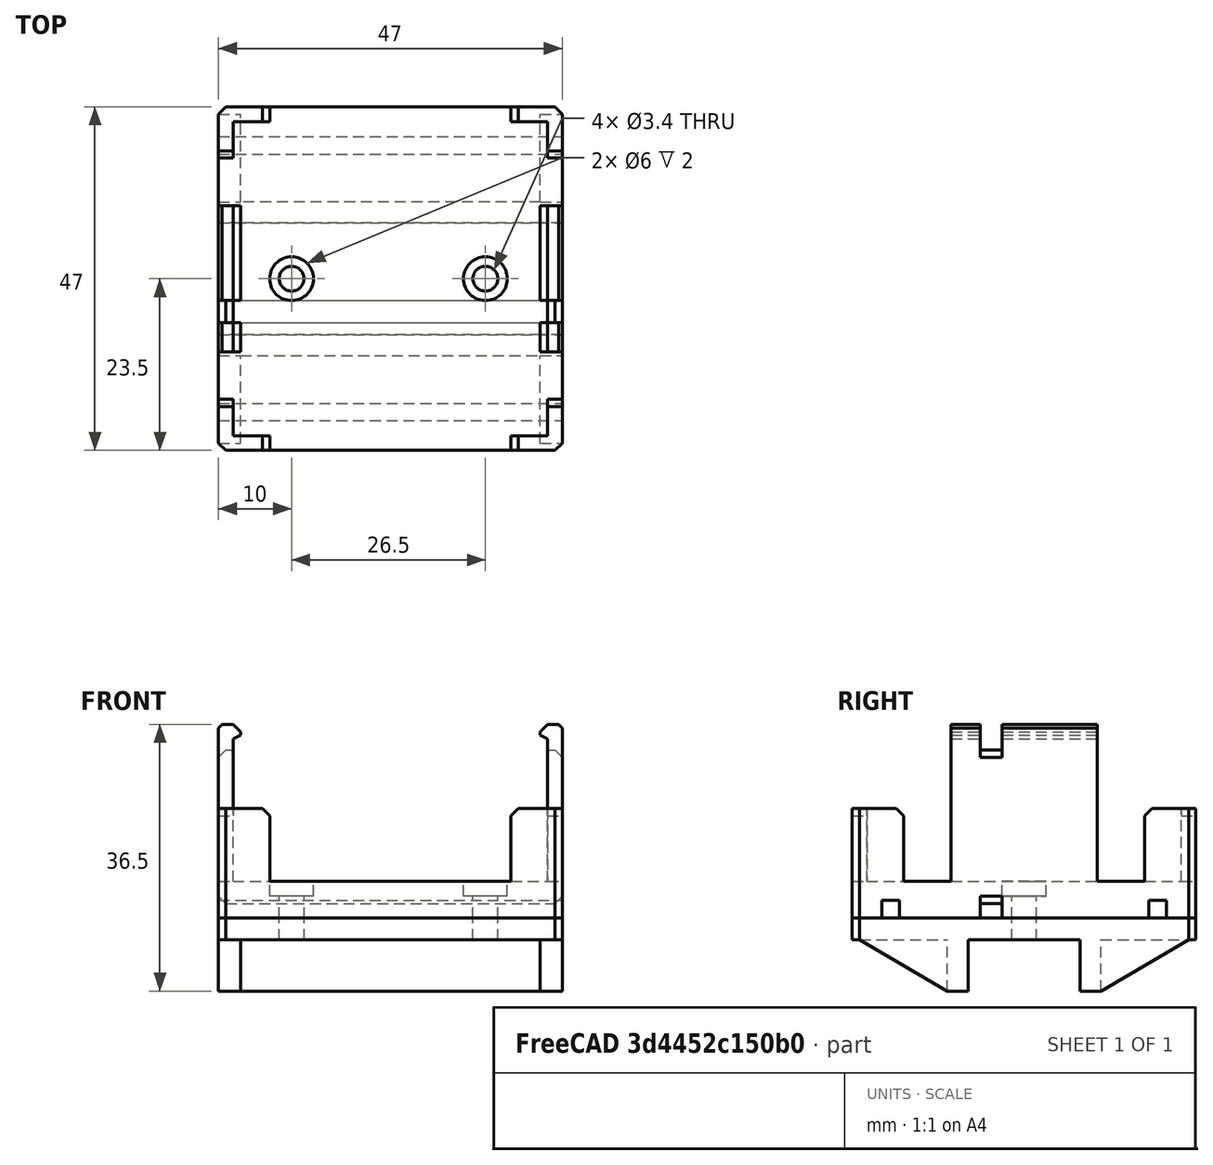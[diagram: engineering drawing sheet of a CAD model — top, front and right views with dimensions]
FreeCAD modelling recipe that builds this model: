
FCSTD DOCUMENT  (FreeCAD 0.18R16146 (Git))
Label: sonoff-mount
License: All rights reserved
LicenseURL: http://en.wikipedia.org/wiki/All_rights_reserved
objects: Part::Box×8, Part::MultiFuse×4, Part::Chamfer×3, Part::Cylinder×2, Part::Cut×2, Part::Feature×1
note: 20 computed .brp shape members not serialized (recipe doc carries the construction recipe); baked Part::Feature solids carry a one-line shape summary decoded from their .brp

FEATURE [Part::Feature] Cut001001  label="sonoff-mounter001"
  Placement = pos=(37.5,27,-3) rot=(0,0,-1;1.5708rad)
  shape: bbox 47 x 47 x 26.5 mm, 92 faces (baked)
FEATURE [Part::Box] Box  label="Cube"
  AttacherType = Attacher::AttachEngine3D
  Height = 3
  Length = 47
  Placement = pos=(-24.5,-20,-3) rot=(0,0,1;0rad)
  Width = 47
FEATURE [Part::Box] Box001  label="Cube001"
  AttacherType = Attacher::AttachEngine3D
  Height = 10
  Length = 47
  Placement = pos=(-24.5,11,-10) rot=(0,0,1;0rad)
  Width = 3
FEATURE [Part::Box] Box002  label="Cube002"
  AttacherType = Attacher::AttachEngine3D
  Height = 10
  Length = 47
  Placement = pos=(-24.5,-7,-10) rot=(0,0,1;0rad)
  Width = 3
FEATURE [Part::Chamfer] Chamfer
  Base = -> Box
  Edges = 4 edges r=1: [Edge1,Edge3,Edge5,Edge7]
FEATURE [Part::Box] Box003  label="Cube003"
  AttacherType = Attacher::AttachEngine3D
  Height = 10
  Length = 3
  Placement = pos=(-24.5,11,-10) rot=(0,0,1;0rad)
  Width = 15
FEATURE [Part::Box] Box004  label="Cube004"
  AttacherType = Attacher::AttachEngine3D
  Height = 10
  Length = 3
  Placement = pos=(-24.5,-19,-10) rot=(0,0,1;0rad)
  Width = 15
FEATURE [Part::Box] Box005  label="Cube005"
  AttacherType = Attacher::AttachEngine3D
  Height = 10
  Length = 3
  Placement = pos=(19.5,-19,-10) rot=(0,0,1;0rad)
  Width = 15
FEATURE [Part::Box] Box006  label="Cube006"
  AttacherType = Attacher::AttachEngine3D
  Height = 10
  Length = 3
  Placement = pos=(19.5,11,-10) rot=(0,0,1;0rad)
  Width = 15
FEATURE [Part::MultiFuse] Fusion
  Shapes = -> [Box005,Box004]
FEATURE [Part::Chamfer] Chamfer001
  Base = -> Fusion
  Edges = 2 edges: [Edge9 r1=7 r2=12,Edge21 r1=7 r2=12]
FEATURE [Part::MultiFuse] Fusion001
  Shapes = -> [Box003,Box006]
FEATURE [Part::Chamfer] Chamfer002
  Base = -> Fusion001
  Edges = 2 edges: [Edge11 r1=7 r2=12,Edge23 r1=7 r2=12]
FEATURE [Part::Cylinder] Cylinder
  Angle = 360
  AttacherType = Attacher::AttachEngine3D
  Height = 10
  Placement = pos=(-14.5,3.5,-4) rot=(0,0,1;0rad)
  Radius = 1.7
FEATURE [Part::Cylinder] Cylinder001
  Angle = 360
  AttacherType = Attacher::AttachEngine3D
  Height = 10
  Placement = pos=(12,3.5,-4) rot=(0,0,1;0rad)
  Radius = 1.7
FEATURE [Part::MultiFuse] Fusion002
  Shapes = -> [Cylinder,Cylinder001]
FEATURE [Part::Cut] Cut
  Base = -> Chamfer
  Tool = -> Fusion002
FEATURE [Part::MultiFuse] Fusion003
  Shapes = -> [Cut,Chamfer002,Chamfer001,Box002,Box001]
FEATURE [Part::Box] Box007  label="Cube007"
  AttacherType = Attacher::AttachEngine3D
  Height = 10
  Length = 60
  Placement = pos=(-32,-4.15,-13) rot=(0,0,1;0rad)
  Width = 15.3
FEATURE [Part::Cut] Cut001002
  Base = -> Fusion003
  Tool = -> Box007
